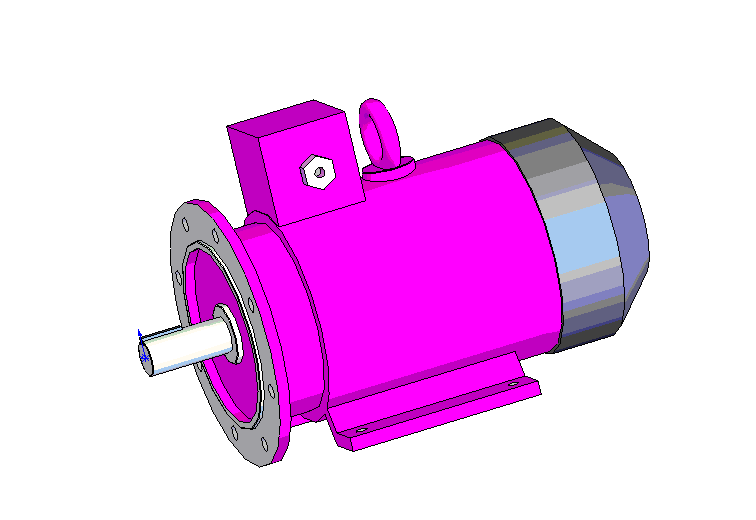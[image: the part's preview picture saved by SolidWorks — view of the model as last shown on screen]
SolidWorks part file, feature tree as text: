
SOLIDWORKS PART (.sldprt)
format: sldprt  version: not decoded by parser v0  size: 723,456 bytes
history: native  units: mm
features: sketch x18, extrude x12, plane x4, cut_extrude x4, chamfer x3, material x1, sweep x1 (+10 scaffold rows collapsed)
feature tree (53):
  scaffold x10  (default folders/planes/origin — collapsed)
  material  "Ст.3 ГОСТ 380-88"
  plane  "Спереди"
  plane  "Сверху"
  plane  "Справа"
  sketch  "Эскиз1"  dims[D1=48.0mm]
  extrude  "Вытянуть1"  Depth=110mm
  sketch  "Эскиз2"  dims[D1=9.0mm D2=9.0mm D3=51.5mm]
  extrude  "Вытянуть2"  Depth=55mm
  sketch  "Эскиз3"  dims[D1=350.0mm]
  extrude  "Вытянуть3"  Depth=15mm
  sketch  "Эскиз4"  dims[D1=250.0mm D2=232.0mm]
  extrude  "Вытянуть4"  Depth=5mm
  sketch  "Эскиз5"  dims[D1=232.0mm D2=80.0mm]
  cut_extrude  "Вырез-Вытянуть1"  Depth=8mm
  chamfer  "Фаска1"  Distance=1mm Angle=45deg
  sketch  "Эскиз6"  dims[c1.D2=19.0mm c1.D1=~222.342459mm c2.D1=22.5deg c2.D3=150.0mm c2.D4=150.0mm c2.D5=150.0mm]
  cut_extrude  "Вырез-Вытянуть2"  [1 undecoded]
  sketch  "Эскиз7"  dims[D1=250.0mm]
  extrude  "Вытянуть5"  Depth=68mm
  sketch  "Эскиз8"  dims[D1=280.0mm]
  extrude  "Вытянуть6"  Depth=322mm
  sketch  "Эскиз9"  dims[D1=288.0mm]
  extrude  "Вытянуть7"  Depth=145mm
  chamfer  "Фаска2"  Distance=60mm Angle=45deg
  sketch  "Эскиз10"  dims[c1.D1=18.0mm c1.D2=18.0mm c1.D3=~100.823354mm c2.D3=30.0deg c2.D4=50.0mm c2.D5=152.0mm c2.D6=160.0mm c2.D7=~105.04342mm]
  extrude  "Вытянуть8"  Depth=260mm
  sketch  "Эскиз11"  dims[c1.D2=15.0mm c1.D1=218.0mm c1.D3=127.0mm c1.D4=90.0deg c1.D5=396.0mm c1.D6=254.0mm c1.D7=178.0mm c2.D5=210.0mm c2.D7=428.0mm]
  cut_extrude  "Вырез-Вытянуть3"  [1 undecoded]
  sketch  "Эскиз12"  dims[D1=120.0mm D2=120.0mm D3=1.0mm]
  extrude  "Вытянуть9"  Depth=245mm
  sketch  "Эскиз13"  dims[D1=70.0mm D2=370.0mm]
  extrude  "Вытянуть10"  Depth=150mm
  chamfer  "Фаска3"  Distance=1mm Angle=45deg
  plane  "Плоскость1"  Offset=370mm
  sketch  "Эскиз14"  dims[D1=76.0mm]
  sketch  "Эскиз15"  dims[D1=24.0mm D2=76.0mm]
  sweep  "По траектории1"
  sketch  "Эскиз16"  dims[D1=32.0mm D2=60.0mm D3=60.0mm]
  extrude  "Вытянуть11"  Depth=14mm
  sketch  "Эскиз17"  dims[D1=19.5mm]
  extrude  "Вытянуть12"  Depth=16mm
  sketch  "Эскиз18"  dims[D1=14.0mm]
  cut_extrude  "Вырез-Вытянуть4"  Depth=16mm
decode coverage: 35 of 38 modeling features carry decoded parameters
note: ~ marks probable driven/reference dimensions
note: 2 parameter values undecoded
note: suppression state not decoded; provenance and decode notes live in map.json
